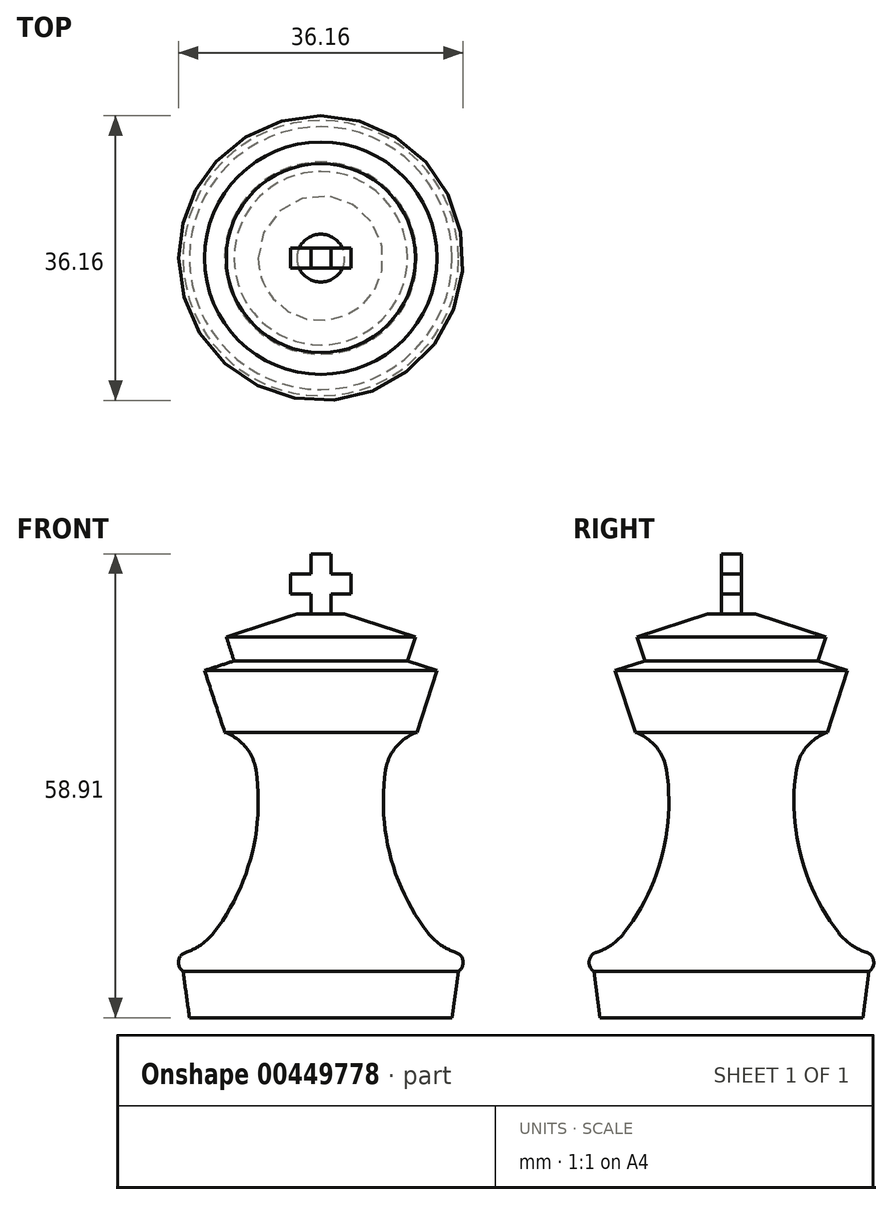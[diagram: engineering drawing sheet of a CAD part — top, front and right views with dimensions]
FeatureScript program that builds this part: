
annotation { "Feature Type Name" : "Feature", "Feature Type Description" : "" }
export const myFeature = defineFeature(function(context is Context, id is Id, definition is map)
    precondition{}
    {
        {
            var Q0;
            Q0=qCreatedBy(makeId("Front.planeOp"),FACE);
            var sketch = newSketch(context, id + "F0", { "sketchPlane" : qUnion([Q0])});
            skLineSegment(sketch, "E0", {"start": v(-10.86, -28.1) * mm, "end": v(5.83, -28.1) * mm});
            skLineSegment(sketch, "E1", {"start": v(-10.86, -28.1) * mm, "end": v(-10.86, 23.18) * mm});
            skLineSegment(sketch, "E2", {"start": v(-7.82, 23.18) * mm, "end": v(1.14, 20.25) * mm});
            skLineSegment(sketch, "E3", {"start": v(1.14, 20.25) * mm, "end": v(0.15, 17.21) * mm});
            skLineSegment(sketch, "E4", {"start": v(0.15, 17.21) * mm, "end": v(3.9, 15.99) * mm});
            skLineSegment(sketch, "E5", {"start": v(3.9, 15.99) * mm, "end": v(1.34, 8.13) * mm});
            skArc(sketch, "E6", {"start": v(1.34, 8.13) * mm, "mid": v(-1.3, 6.3) * mm, "end": v(-2.61, 3.37) * mm});
            skArc(sketch, "E7", {"start": v(-2.61, 3.37) * mm, "mid": v(-2.04, -7.54) * mm, "end": v(2.77, -17.35) * mm});
            skArc(sketch, "E8", {"start": v(2.77, -17.35) * mm, "mid": v(4.34, -18.85) * mm, "end": v(6.28, -19.8) * mm});
            skArc(sketch, "E9", {"start": v(6.28, -19.8) * mm, "mid": v(7.2, -20.9) * mm, "end": v(6.63, -22.2) * mm});
            skLineSegment(sketch, "E10", {"start": v(6.63, -22.2) * mm, "end": v(5.83, -28.1) * mm});
            skLineSegment(sketch, "E11", {"start": v(-7.82, 23.18) * mm, "end": v(-10.86, 23.18) * mm});
            skLineSegment(sketch, "E12", {"start": v(-10.86, 23.18) * mm, "end": v(-10.86, 30.8) * mm, "construction": true});
            skLineSegment(sketch, "E13", {"start": v(-10.86, 30.8) * mm, "end": v(-9.59, 30.8) * mm});
            skLineSegment(sketch, "E14", {"start": v(-9.59, 30.8) * mm, "end": v(-9.59, 28.26) * mm});
            skLineSegment(sketch, "E15", {"start": v(-9.59, 28.26) * mm, "end": v(-7.05, 28.26) * mm});
            skLineSegment(sketch, "E16", {"start": v(-7.05, 28.26) * mm, "end": v(-7.05, 25.72) * mm});
            skLineSegment(sketch, "E17", {"start": v(-7.05, 25.72) * mm, "end": v(-9.59, 25.72) * mm});
            skLineSegment(sketch, "E18", {"start": v(-9.59, 25.72) * mm, "end": v(-9.59, 23.18) * mm});
            skLineSegment(sketch, "E19.MirrorCS", {"start": v(-10.86, 30.8) * mm, "end": v(-12.13, 30.8) * mm});
            skLineSegment(sketch, "E20.MirrorCS", {"start": v(-12.13, 30.8) * mm, "end": v(-12.13, 28.26) * mm});
            skLineSegment(sketch, "E21.MirrorCS", {"start": v(-12.13, 28.26) * mm, "end": v(-14.67, 28.26) * mm});
            skLineSegment(sketch, "E22.MirrorCS", {"start": v(-14.67, 28.26) * mm, "end": v(-14.67, 25.72) * mm});
            skLineSegment(sketch, "E23.MirrorCS", {"start": v(-12.13, 25.72) * mm, "end": v(-12.13, 23.18) * mm});
            skLineSegment(sketch, "E24.MirrorCS", {"start": v(-14.67, 25.72) * mm, "end": v(-12.13, 25.72) * mm});
            skLineSegment(sketch, "E25.MirrorCS", {"start": v(-12.13, 23.18) * mm, "end": v(-10.86, 23.18) * mm});
            skPoint(sketch, "E26.orphan", {"position": v(-13.9, 23.18) * mm});
            skSolve(sketch);
        }
        {
            var Q0;
            Q0=makeQuery(id+"F0.imprint","IMPRINT",FACE,{"disambiguationData":[TD([[makeQuery(id+"F0.imprint","IMPRINT",EDGE,{"derivedFrom":sQuery(id+"F0.wireOp",EDGE,"E0")}),1.0]])]});
            var Q1;
            Q1=sQuery(id+"F0.wireOp",EDGE,"E1");
            revolve(context, id + "F1", {"entities" : qUnion([Q0]), "axis" : qUnion([Q1]), "revolveType" : RevolveType.FULL});
        }
        {
            var Q0;
            Q0=makeQuery(id+"F0.imprint","IMPRINT",FACE,{"disambiguationData":[TD([[makeQuery(id+"F0.imprint","IMPRINT",EDGE,{"derivedFrom":sQuery(id+"F0.wireOp",EDGE,"E13")}),-1.0]])]});
            extrude(context, id + "F2", {"entities" : qUnion([Q0]), "operationType" : NewBodyOperationType.ADD, "endBound" : BoundingType.SYMMETRIC, "depth" : 2.54 * mm});
        }
    });
